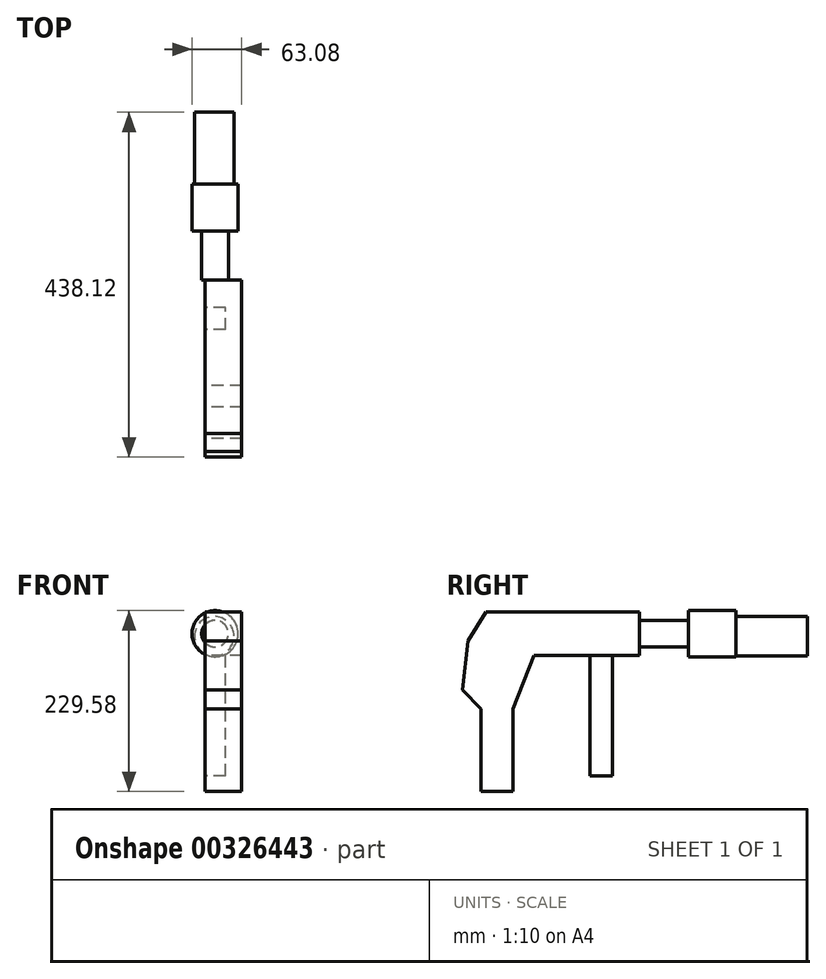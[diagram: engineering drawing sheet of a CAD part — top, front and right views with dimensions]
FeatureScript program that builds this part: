
annotation { "Feature Type Name" : "Feature", "Feature Type Description" : "" }
export const myFeature = defineFeature(function(context is Context, id is Id, definition is map)
    precondition{}
    {
        {
            var Q0;
            Q0=qCreatedBy(makeId("Right.planeOp"),FACE);
            var sketch = newSketch(context, id + "F0", { "sketchPlane" : qUnion([Q0])});
            skLineSegment(sketch, "E0.bottom", {"start": v(-81.9, 47.75) * mm, "end": v(52.3, 47.75) * mm});
            skLineSegment(sketch, "E0.top", {"start": v(-81.9, -7.13) * mm, "end": v(52.3, -7.13) * mm});
            skLineSegment(sketch, "E0.left", {"start": v(-81.9, 47.75) * mm, "end": v(-81.9, -7.13) * mm});
            skLineSegment(sketch, "E0.right", {"start": v(52.3, 47.75) * mm, "end": v(52.3, -7.13) * mm});
            skLineSegment(sketch, "E1", {"start": v(-81.9, 47.75) * mm, "end": v(-142.82, 47.75) * mm});
            skLineSegment(sketch, "E2", {"start": v(-142.82, 47.75) * mm, "end": v(-165.61, 11.07) * mm});
            skLineSegment(sketch, "E3", {"start": v(-165.61, 11.07) * mm, "end": v(-172.7, -51.1) * mm});
            skLineSegment(sketch, "E4", {"start": v(-172.7, -51.1) * mm, "end": v(-149.02, -75.34) * mm});
            skLineSegment(sketch, "E5", {"start": v(-149.02, -75.34) * mm, "end": v(-108.82, -75.34) * mm});
            skLineSegment(sketch, "E6", {"start": v(-108.82, -75.34) * mm, "end": v(-81.9, -7.13) * mm});
            skSolve(sketch);
        }
        {
            var Q0;
            Q0=makeQuery(id+"F0.imprint","IMPRINT",FACE,{"disambiguationData":[TD([[makeQuery(id+"F0.imprint","IMPRINT",EDGE,{"derivedFrom":sQuery(id+"F0.wireOp",EDGE,"E0.left")}),-1.0]])]});
            var Q1;
            Q1=makeQuery(id+"F0.imprint","IMPRINT",FACE,{"disambiguationData":[TD([[makeQuery(id+"F0.imprint","IMPRINT",EDGE,{"derivedFrom":sQuery(id+"F0.wireOp",EDGE,"E0.bottom")}),-1.0]])]});
            extrude(context, id + "F1", {"entities" : qUnion([Q0, Q1]), "depth" : 25.4 * mm});
        }
        {
            var Q0;
            Q0=makeQuery(id+"F1.opExtrude","SWEPT_FACE",FACE,{"disambiguationData":[OSD([sQuery(id+"F0.wireOp",EDGE,"E0.right")])]});
            var sketch = newSketch(context, id + "F2", { "sketchPlane" : qUnion([Q0])});
            skCircle(sketch, "E7", {"center": v(-12.7, 20.3) * mm, "radius": 16.92 * mm});
            skPoint(sketch, "E7.centerSnap0", {"position": v(0, 20.3) * mm});
            skPoint(sketch, "E7.centerSnap1", {"position": v(-12.7, 47.75) * mm});
            skSolve(sketch);
        }
        {
            var Q0;
            Q0 = qSketchRegion(id + "F2", true);
            extrude(context, id + "F3", {"entities" : qUnion([Q0]), "operationType" : NewBodyOperationType.ADD, "depth" : 62.23 * mm});
        }
        {
            var Q0;
            Q0=makeQuery(id+"F3.opExtrude","CAP_FACE",FACE,{"disambiguationData":[OSD([sQuery(id+"F2.wireOp",EDGE,"E7")])],"isStart":false});
            var sketch = newSketch(context, id + "F4", { "sketchPlane" : qUnion([Q0])});
            skCircle(sketch, "E8", {"center": v(-12.7, 20.3) * mm, "radius": 29.3 * mm});
            skSolve(sketch);
        }
        {
            var Q0;
            Q0 = qSketchRegion(id + "F4", true);
            extrude(context, id + "F5", {"entities" : qUnion([Q0]), "operationType" : NewBodyOperationType.ADD, "depth" : 59.94 * mm});
        }
        {
            var Q0;
            Q0=makeQuery(id+"F0.imprint","IMPRINT",FACE,{"disambiguationData":[TD([[makeQuery(id+"F0.imprint","IMPRINT",EDGE,{"derivedFrom":sQuery(id+"F0.wireOp",EDGE,"E0.left")}),-1.0]])]});
            var Q1;
            Q1=makeQuery(id+"F0.imprint","IMPRINT",FACE,{"disambiguationData":[TD([[makeQuery(id+"F0.imprint","IMPRINT",EDGE,{"derivedFrom":sQuery(id+"F0.wireOp",EDGE,"E0.bottom")}),-1.0]])]});
            extrude(context, id + "F6", {"entities" : qUnion([Q0, Q1]), "operationType" : NewBodyOperationType.ADD, "depth" : 46.48 * mm});
        }
        {
            var Q0;
            {var subQ0=sQuery(id+"F0.wireOp",EDGE,"E0.top");Q0=makeQuery(id+"F6.boolean.opBoolean","MERGE",FACE,{"derivedFrom":[makeQuery(id+"F1.opExtrude","SWEPT_FACE",FACE,{"disambiguationData":[OSD([subQ0])]}),makeQuery(id+"F6.opExtrude","SWEPT_FACE",FACE,{"disambiguationData":[OSD([subQ0])]})]});}
            var sketch = newSketch(context, id + "F7", { "sketchPlane" : qUnion([Q0])});
            skCircle(sketch, "E9", {"center": v(24.26, 4.57) * mm, "radius": 9.62 * mm});
            skSolve(sketch);
        }
        {
            var Q0;
            Q0=makeQuery(id+"F7.imprint","IMPRINT",FACE,{"disambiguationData":[TD([[makeQuery(id+"F7.imprint","IMPRINT",EDGE,{"derivedFrom":sQuery(id+"F7.wireOp",EDGE,"E9")}),-1.0]])]});
            var sketch = newSketch(context, id + "F8", { "sketchPlane" : qUnion([Q0])});
            skLineSegment(sketch, "E10.bottom", {"start": v(25.88, 10.76) * mm, "end": v(0, 10.76) * mm});
            skLineSegment(sketch, "E10.top", {"start": v(25.88, -17.5) * mm, "end": v(0, -17.5) * mm});
            skLineSegment(sketch, "E10.left", {"start": v(25.88, 10.76) * mm, "end": v(25.88, -17.5) * mm});
            skLineSegment(sketch, "E10.right", {"start": v(0, 10.76) * mm, "end": v(0, -17.5) * mm});
            skSolve(sketch);
        }
        {
            var Q0;
            Q0 = qSketchRegion(id + "F8", true);
            extrude(context, id + "F9", {"entities" : qUnion([Q0]), "operationType" : NewBodyOperationType.ADD, "depth" : 153.16 * mm});
        }
        {
            var Q0;
            Q0=makeQuery(id+"F5.opExtrude","CAP_FACE",FACE,{"disambiguationData":[OSD([sQuery(id+"F4.wireOp",EDGE,"E8")])],"isStart":false});
            var sketch = newSketch(context, id + "F10", { "sketchPlane" : qUnion([Q0])});
            skSolve(sketch);
        }
        {
            var Q0;
            Q0=makeQuery(id+"F10.imprint","IMPRINT",FACE,{"disambiguationData":[TD([[makeQuery(id+"F10.imprint","IMPRINT",EDGE,{"derivedFrom":makeQuery(id+"F5.opExtrude","CAP_EDGE",EDGE,{"disambiguationData":[OSD([sQuery(id+"F4.wireOp",EDGE,"E8")])],"isStart":false})}),1.0]])]});
            var sketch = newSketch(context, id + "F11", { "sketchPlane" : qUnion([Q0])});
            skCircle(sketch, "E11", {"center": v(-11.6, 17.18) * mm, "radius": 25.11 * mm});
            skSolve(sketch);
        }
        {
            var Q0;
            Q0 = qSketchRegion(id + "F11", true);
            extrude(context, id + "F12", {"entities" : qUnion([Q0]), "operationType" : NewBodyOperationType.ADD, "depth" : 90.93 * mm});
        }
        {
            var Q0;
            {var subQ0=sQuery(id+"F0.wireOp",EDGE,"E5");Q0=makeQuery(id+"F6.boolean.opBoolean","MERGE",FACE,{"derivedFrom":[makeQuery(id+"F1.opExtrude","SWEPT_FACE",FACE,{"disambiguationData":[OSD([subQ0])]}),makeQuery(id+"F6.opExtrude","SWEPT_FACE",FACE,{"disambiguationData":[OSD([subQ0])]})]});}
            extrude(context, id + "F13", {"entities" : qUnion([Q0]), "operationType" : NewBodyOperationType.ADD, "depth" : 104.65 * mm});
        }
    });
